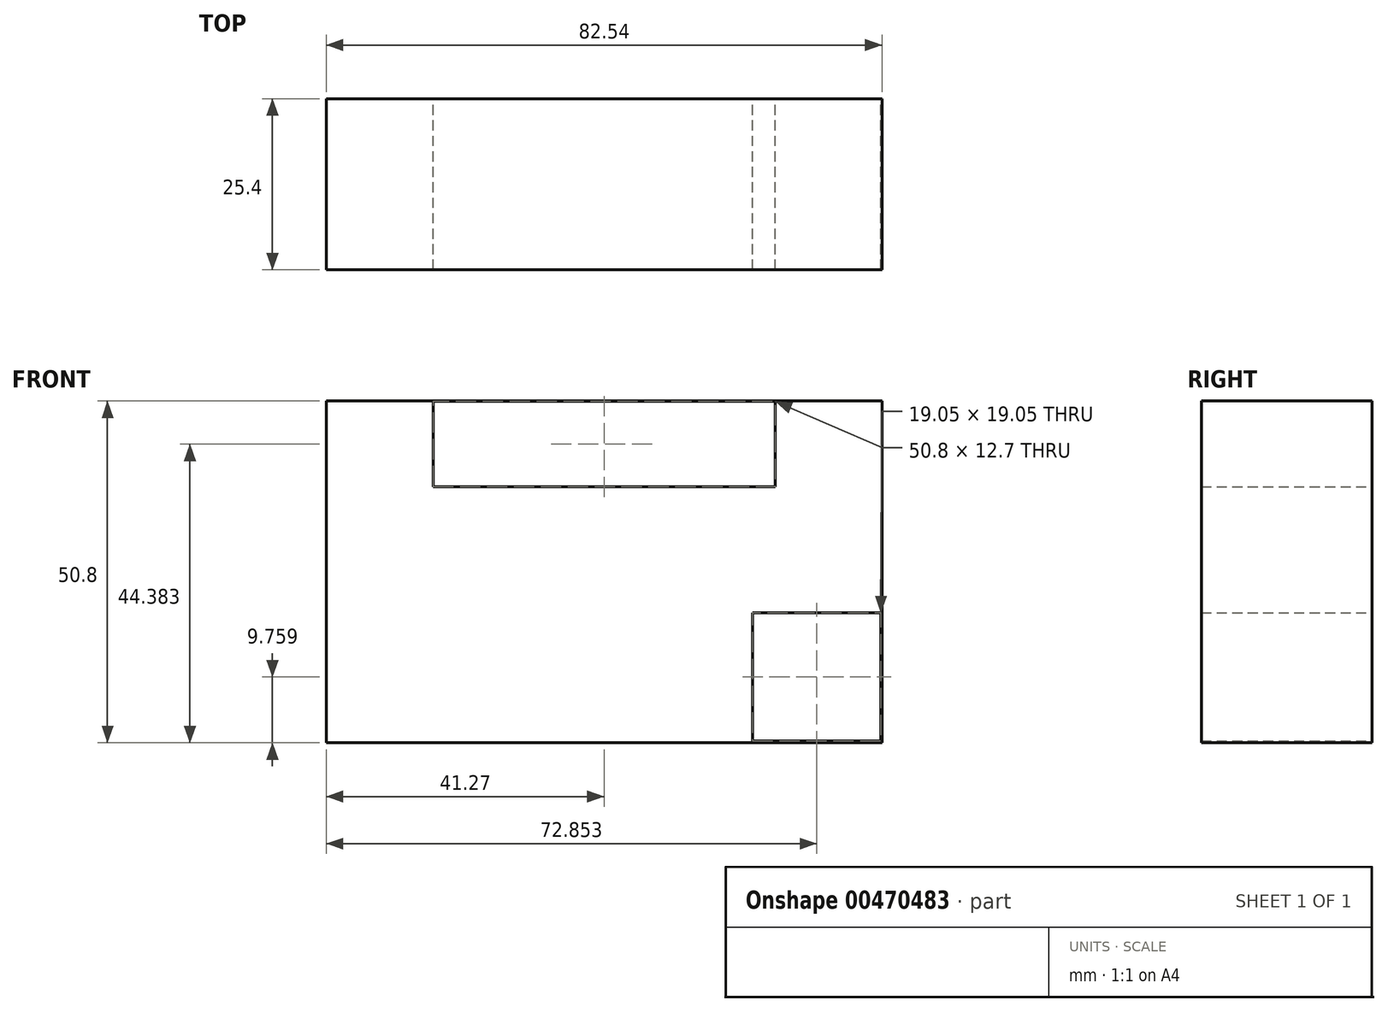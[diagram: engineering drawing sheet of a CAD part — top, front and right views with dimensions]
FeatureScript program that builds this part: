
annotation { "Feature Type Name" : "Feature", "Feature Type Description" : "" }
export const myFeature = defineFeature(function(context is Context, id is Id, definition is map)
    precondition{}
    {
        {
            var Q0;
            Q0=qCreatedBy(makeId("Front.planeOp"),FACE);
            var sketch = newSketch(context, id + "F0", { "sketchPlane" : qUnion([Q0])});
            skLineSegment(sketch, "E0.bottom", {"start": v(41.27, -25.4) * mm, "end": v(-41.28, -25.4) * mm});
            skLineSegment(sketch, "E0.top", {"start": v(41.27, 25.4) * mm, "end": v(-41.28, 25.4) * mm});
            skLineSegment(sketch, "E0.left", {"start": v(41.27, -25.4) * mm, "end": v(41.27, 25.4) * mm});
            skLineSegment(sketch, "E0.right", {"start": v(-41.28, -25.4) * mm, "end": v(-41.28, 25.4) * mm});
            skPoint(sketch, "E0.middle", {"position": v(0, 0) * mm});
            skSolve(sketch);
        }
        {
            var Q0;
            Q0=makeQuery(id+"F0.imprint","IMPRINT",FACE,{"disambiguationData":[TD([[makeQuery(id+"F0.imprint","IMPRINT",EDGE,{"derivedFrom":sQuery(id+"F0.wireOp",EDGE,"E0.bottom")}),-1.0]])]});
            extrude(context, id + "F1", {"entities" : qUnion([Q0]), "depth" : 25.4 * mm});
        }
        {
            var Q0;
            Q0=qCreatedBy(makeId("Front.planeOp"),FACE);
            var sketch = newSketch(context, id + "F2", { "sketchPlane" : qUnion([Q0])});
            skLineSegment(sketch, "E1.bottom", {"start": v(-25.4, 25.33) * mm, "end": v(25.4, 25.33) * mm});
            skLineSegment(sketch, "E1.top", {"start": v(-25.4, 12.63) * mm, "end": v(25.4, 12.63) * mm});
            skLineSegment(sketch, "E1.left", {"start": v(-25.4, 25.33) * mm, "end": v(-25.4, 12.63) * mm});
            skLineSegment(sketch, "E1.right", {"start": v(25.4, 25.33) * mm, "end": v(25.4, 12.63) * mm});
            skPoint(sketch, "E1.middle", {"position": v(0, 18.98) * mm});
            skSolve(sketch);
        }
        {
            var Q0;
            Q0 = qSketchRegion(id + "F2", true);
            extrude(context, id + "F3", {"entities" : qUnion([Q0]), "operationType" : NewBodyOperationType.REMOVE, "depth" : 50.3 * mm});
        }
        {
            var Q0;
            Q0=qCreatedBy(makeId("Front.planeOp"),FACE);
            var sketch = newSketch(context, id + "F4", { "sketchPlane" : qUnion([Q0])});
            skLineSegment(sketch, "E2.bottom", {"start": v(41.1, -25.17) * mm, "end": v(22.06, -25.17) * mm});
            skLineSegment(sketch, "E2.top", {"start": v(41.1, -6.12) * mm, "end": v(22.06, -6.12) * mm});
            skLineSegment(sketch, "E2.left", {"start": v(41.1, -25.17) * mm, "end": v(41.1, -6.12) * mm});
            skLineSegment(sketch, "E2.right", {"start": v(22.06, -25.17) * mm, "end": v(22.06, -6.12) * mm});
            skPoint(sketch, "E2.middle", {"position": v(31.58, -15.64) * mm});
            skSolve(sketch);
        }
        {
            var Q0;
            Q0 = qSketchRegion(id + "F4", true);
            extrude(context, id + "F5", {"entities" : qUnion([Q0]), "operationType" : NewBodyOperationType.REMOVE, "depth" : 72.64 * mm});
        }
    });
